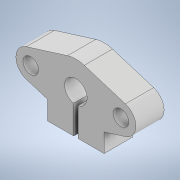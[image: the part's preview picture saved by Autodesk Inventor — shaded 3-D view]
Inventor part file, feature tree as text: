
AUTODESK INVENTOR PART (.ipt)
format: ipt  version: 2020 (Build 240168000, 168)  size: 136,704 bytes
history: native  units: mm
features: extrude x1, sketch x1
ambient origin geometry x8: Origin, YZ Plane, XZ Plane, XY Plane, X Axis, Y Axis, Z Axis, Center Point
bodies: Solid1 (feature_tree)
feature tree (2):
  extrude  "Extrusion1"  Depth=10.0mm
  sketch  "Sketch1"  dims[d0=5.5mm d1=5.5mm d2=32.0mm d3=16.0mm d4=8.0mm d5=10.5mm d6=10.5mm d7=20.0mm d8=0.0mm d9=0.0mm d10=14.0mm d11=20.0mm d12=10.0mm d13=1.5mm d14=0.75mm d15=10.0mm d16=0.0mm]
